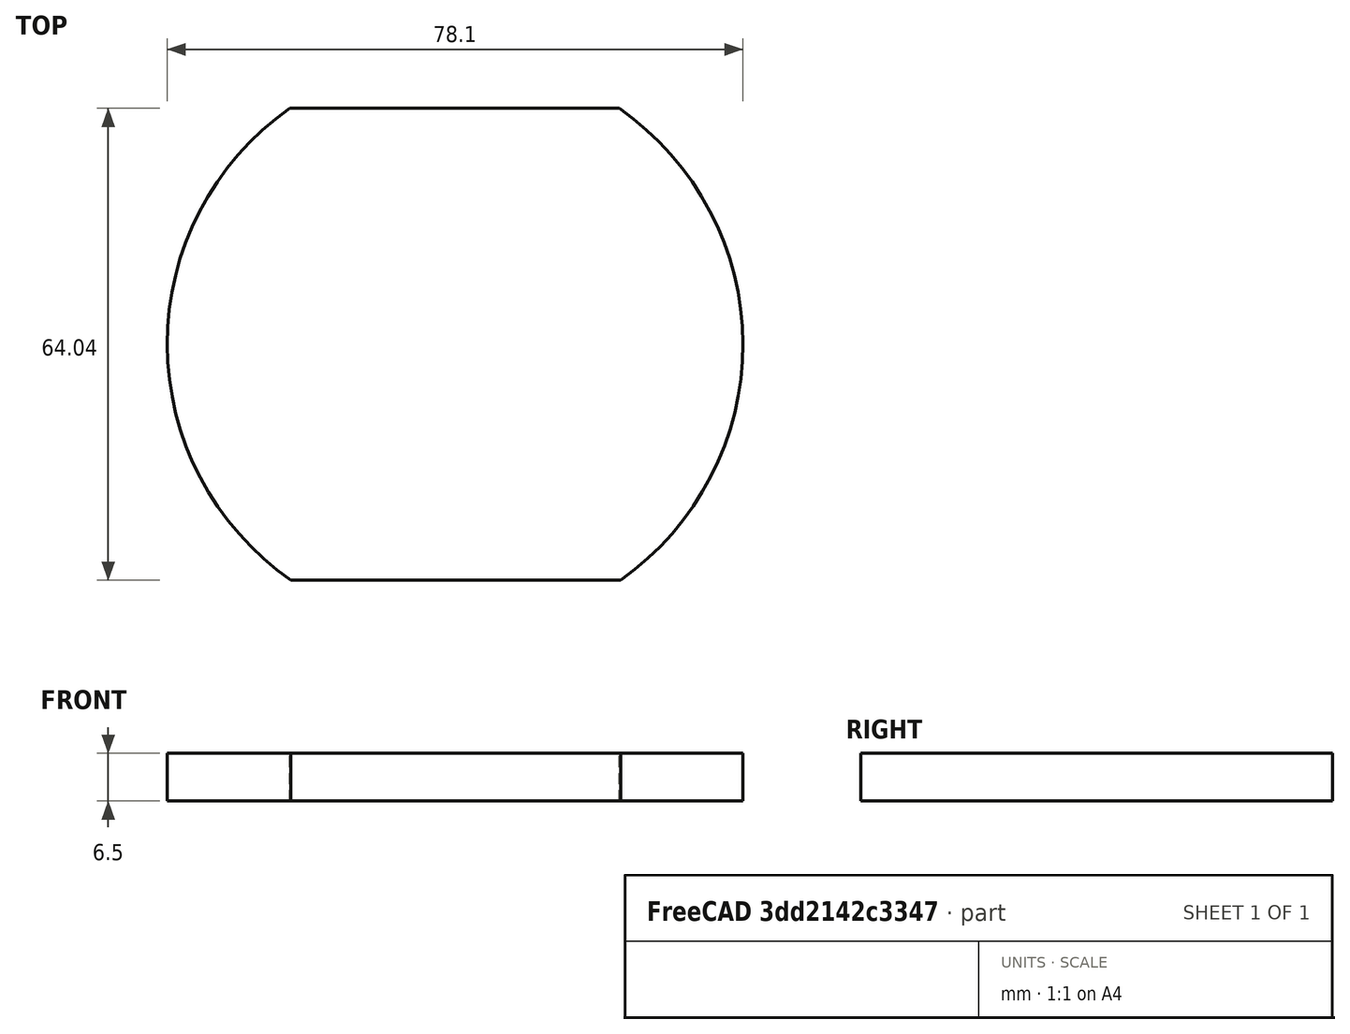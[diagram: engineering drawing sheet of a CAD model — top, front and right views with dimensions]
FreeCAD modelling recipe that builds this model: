
FCSTD DOCUMENT  (FreeCAD 1.0R39319 (Git))
Label: chord_cut_90mm_78mm
License: All rights reserved
LicenseURL: https://en.wikipedia.org/wiki/All_rights_reserved
objects: Sketcher::SketchObject×1, PartDesign::Pad×1, PartDesign::Body×1
note: 6 computed .brp shape members not serialized (recipe doc carries the construction recipe); baked Part::Feature solids carry a one-line shape summary decoded from their .brp

FEATURE [Sketcher::SketchObject] Sketch_1
  ArcFitTolerance = 1e-06
  AttachmentSupport = -> [XY_Plane]
  FullyConstrained = false
  MakeInternals = false
  MapMode = 5
  sketch-geometry (4):
    g0: ArcOfCircle CenterX=-0.00134479 CenterY=-1.52837 CenterZ=0 NormalX=0 NormalY=0 NormalZ=1 AngleXU=0 Radius=39.0544 StartAngle=5.32484 EndAngle=7.24737
    g1: LineSegment StartX=22.263 StartY=30.5581 StartZ=0 EndX=-22.4328 EndY=30.5581 EndZ=0
    g2: ArcOfCircle CenterX=0.00216121 CenterY=-1.40385 CenterZ=0 NormalX=0 NormalY=0 NormalZ=1 AngleXU=0 Radius=39.0499 StartAngle=2.18281 EndAngle=4.10567
    g3: LineSegment StartX=-22.263 StartY=-33.4843 StartZ=0 EndX=22.4499 EndY=-33.4843 EndZ=0
  constraints (7):
    c: Coincident(g0,g1)
    c: Coincident(g1,g2)
    c: Coincident(g2,g3)
    c: Coincident(g3,g0)
    c: Parallel(g1,g3)
    c: Horizontal(g1)
    c: Distance(g1,g3) = 78
FEATURE [PartDesign::Pad] Pad_1
  Direction = (0,0,1)
  Length = 6.5
  Length2 = 10
  Profile = -> Sketch_1
  Refine = true
  Suppressed = false
  Type = 0
FEATURE [PartDesign::Body] Body
  AllowCompound = false
  Group = -> [Sketch_1,Pad_1]
  Origin = -> Origin
  Tip = -> Pad_1
